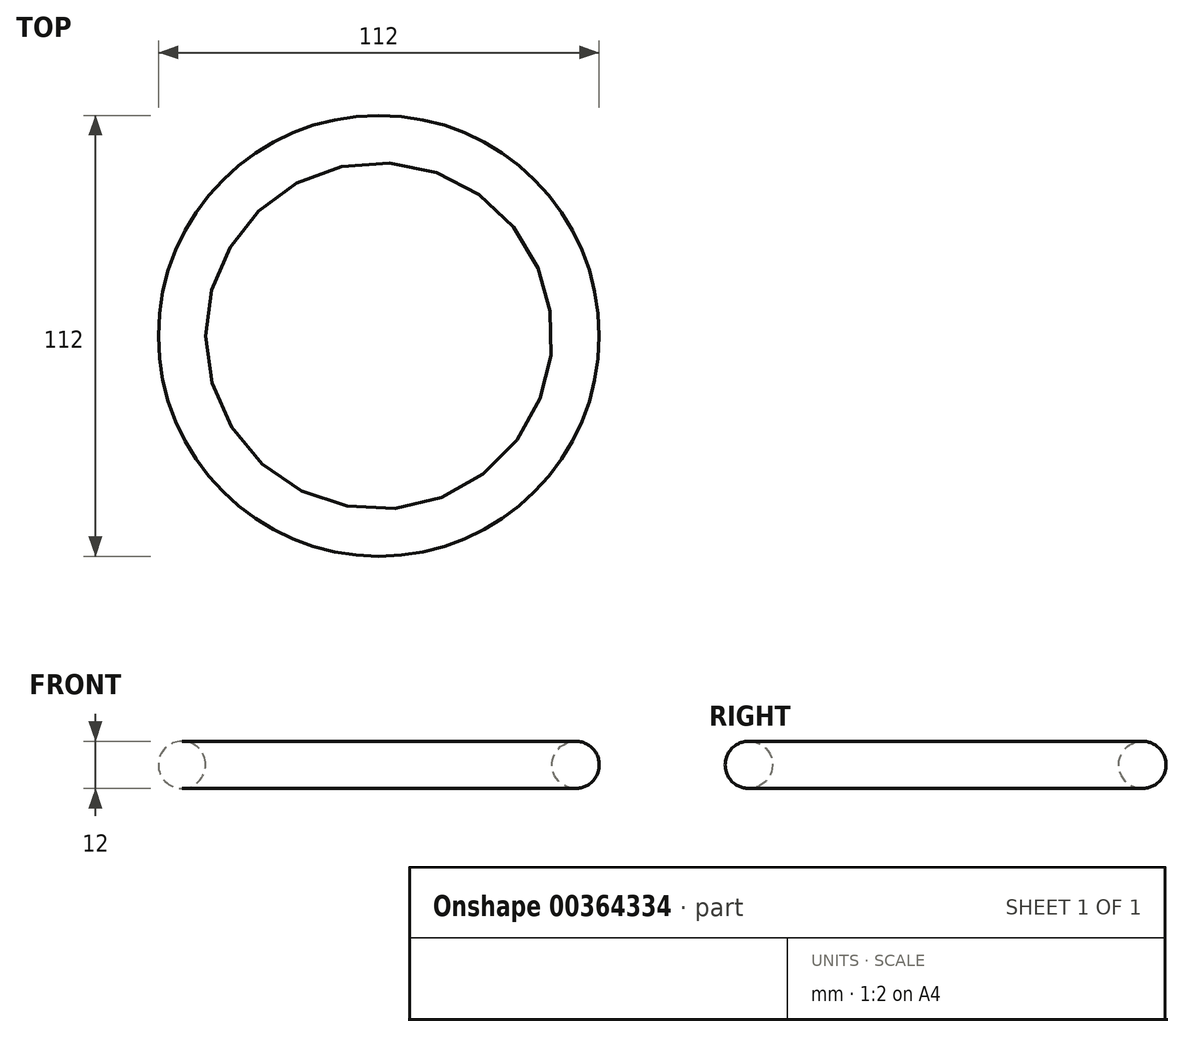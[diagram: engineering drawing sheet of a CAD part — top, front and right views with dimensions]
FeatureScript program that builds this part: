
annotation { "Feature Type Name" : "Feature", "Feature Type Description" : "" }
export const myFeature = defineFeature(function(context is Context, id is Id, definition is map)
    precondition{}
    {
        {
            var Q0;
            Q0=qCreatedBy(makeId("Front.planeOp"),FACE);
            var sketch = newSketch(context, id + "F0", { "sketchPlane" : qUnion([Q0])});
            skCircle(sketch, "E0", {"center": v(-50, 0) * mm, "radius": 6 * mm});
            skLineSegment(sketch, "E1", {"start": v(0, 0) * mm, "end": v(0, 79.56) * mm, "construction": true});
            skSolve(sketch);
        }
        {
            var Q0;
            Q0=makeQuery(id+"F0.imprint","IMPRINT",FACE,{"disambiguationData":[TD([[makeQuery(id+"F0.imprint","IMPRINT",EDGE,{"derivedFrom":sQuery(id+"F0.wireOp",EDGE,"E0")}),1.0]])]});
            var Q1;
            Q1=sQuery(id+"F0.wireOp",EDGE,"E1");
            revolve(context, id + "F1", {"entities" : qUnion([Q0]), "axis" : qUnion([Q1]), "revolveType" : RevolveType.FULL});
        }
    });
